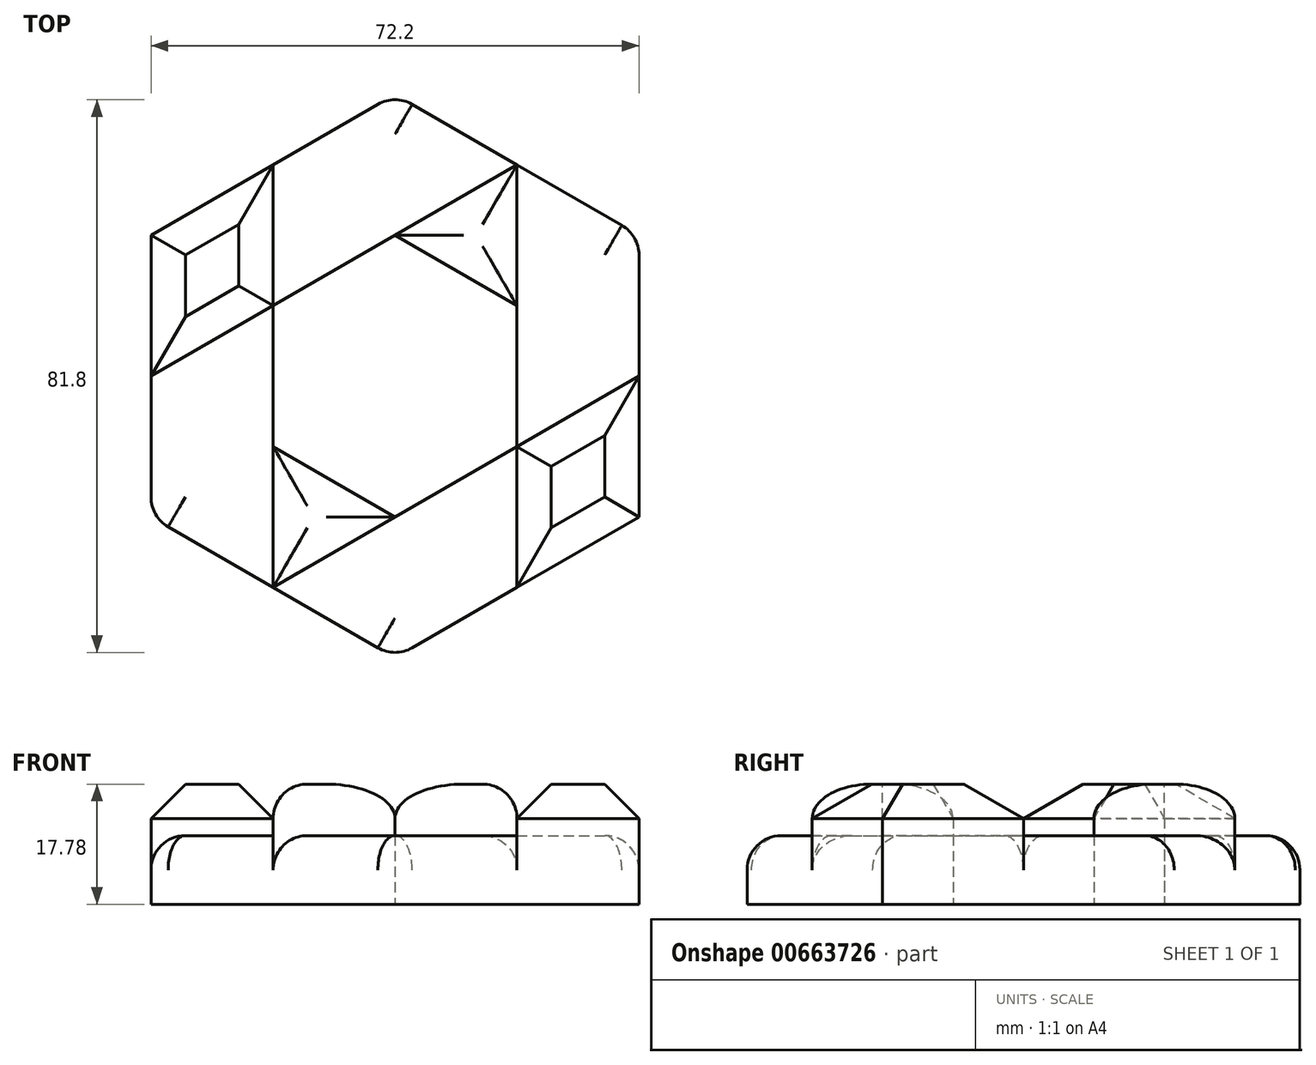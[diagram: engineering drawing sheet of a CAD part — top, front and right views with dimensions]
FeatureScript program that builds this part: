
annotation { "Feature Type Name" : "Feature", "Feature Type Description" : "" }
export const myFeature = defineFeature(function(context is Context, id is Id, definition is map)
    precondition{}
    {
        {
            var Q0;
            Q0=qCreatedBy(makeId("Top.planeOp"),FACE);
            var sketch = newSketch(context, id + "F0", { "sketchPlane" : qUnion([Q0])});
            skCircle(sketch, "E0.cCircle", {"center": v(0, 0) * mm, "radius": 36.1 * mm, "construction": true});
            skLineSegment(sketch, "E0.0", {"start": v(-36.1, -20.84) * mm, "end": v(-36.1, 20.84) * mm});
            skLineSegment(sketch, "E0.1", {"start": v(-36.1, 20.84) * mm, "end": v(0, 41.69) * mm});
            skLineSegment(sketch, "E0.2", {"start": v(0, 41.69) * mm, "end": v(36.1, 20.84) * mm});
            skLineSegment(sketch, "E0.3", {"start": v(36.1, 20.84) * mm, "end": v(36.1, -20.84) * mm});
            skLineSegment(sketch, "E0.4", {"start": v(36.1, -20.84) * mm, "end": v(0, -41.69) * mm});
            skLineSegment(sketch, "E0.5", {"start": v(0, -41.69) * mm, "end": v(-36.1, -20.84) * mm});
            skPoint(sketch, "E0.0.midPoint", {"position": v(-36.1, 0) * mm});
            skCircle(sketch, "E1.cCircle", {"center": v(0, 0) * mm, "radius": 18.05 * mm, "construction": true});
            skLineSegment(sketch, "E1.0", {"start": v(36.1, 0) * mm, "end": v(-18.05, -31.27) * mm});
            skLineSegment(sketch, "E1.1", {"start": v(-18.05, -31.27) * mm, "end": v(-18.05, 31.27) * mm});
            skLineSegment(sketch, "E1.2", {"start": v(-18.05, 31.27) * mm, "end": v(36.1, 0) * mm});
            skPoint(sketch, "E1.0.midPoint", {"position": v(9.03, -15.63) * mm});
            skLineSegment(sketch, "E2.0", {"start": v(-36.1, 0) * mm, "end": v(18.05, 31.27) * mm});
            skLineSegment(sketch, "E2.1", {"start": v(18.05, 31.27) * mm, "end": v(18.05, -31.27) * mm});
            skLineSegment(sketch, "E2.2", {"start": v(18.05, -31.27) * mm, "end": v(-36.1, 0) * mm});
            skPoint(sketch, "E2.0.midPoint", {"position": v(-9.03, 15.63) * mm});
            skSolve(sketch);
        }
        {
            var Q0;
            Q0 = qSketchRegion(id + "F0", true);
            extrude(context, id + "F1", {"entities" : qUnion([Q0]), "depth" : 10.16 * mm, "offsetDistance" : 25.4 * mm});
        }
        {
            var Q0;
            {var subQ1=sQuery(id+"F0.wireOp",EDGE,"E1.0");var subQ3=sQuery(id+"F0.wireOp",EDGE,"E2.2");var subQ4=makeQuery(id+"F0.imprint","INTERSECT",VERTEX,{"derivedFrom":[subQ1,subQ3]});Q0=makeQuery(id+"F0.imprint","IMPRINT",FACE,{"disambiguationData":[TD([[makeQuery(id+"F0.imprint","IMPRINT",EDGE,{"disambiguationData":[TD([[subQ4,-1.0]])],"derivedFrom":subQ3}),1.0]])]});}
            extrude(context, id + "F2", {"entities" : qUnion([Q0]), "operationType" : NewBodyOperationType.ADD, "depth" : 17.78 * mm, "offsetDistance" : 25.4 * mm});
        }
        {
            var Q0;
            {var subQ0=sQuery(id+"F0.wireOp",EDGE,"E2.0");var subQ1=sQuery(id+"F0.wireOp",EDGE,"E1.2");var subQ2=makeQuery(id+"F0.imprint","INTERSECT",VERTEX,{"derivedFrom":[subQ1,subQ0]});Q0=makeQuery(id+"F0.imprint","IMPRINT",FACE,{"disambiguationData":[TD([[makeQuery(id+"F0.imprint","IMPRINT",EDGE,{"disambiguationData":[TD([[subQ2,-1.0]])],"derivedFrom":subQ1}),1.0]])]});}
            extrude(context, id + "F3", {"entities" : qUnion([Q0]), "operationType" : NewBodyOperationType.ADD, "depth" : 17.78 * mm, "offsetDistance" : 25.4 * mm});
        }
        {
            var Q0;
            {var subQ0=sQuery(id+"F0.wireOp",EDGE,"E0.1");var subQ1=sQuery(id+"F0.wireOp",EDGE,"E0.0");var subQ2=makeQuery(id+"F0.imprint","INTERSECT",VERTEX,{"derivedFrom":[subQ1,subQ0]});Q0=makeQuery(id+"F0.imprint","IMPRINT",FACE,{"disambiguationData":[TD([[makeQuery(id+"F0.imprint","IMPRINT",EDGE,{"disambiguationData":[TD([[subQ2,1.0]])],"derivedFrom":subQ1}),-1.0]])]});}
            var Q1;
            {var subQ0=sQuery(id+"F0.wireOp",EDGE,"E0.4");var subQ1=sQuery(id+"F0.wireOp",EDGE,"E0.3");var subQ2=makeQuery(id+"F0.imprint","INTERSECT",VERTEX,{"derivedFrom":[subQ1,subQ0]});Q1=makeQuery(id+"F0.imprint","IMPRINT",FACE,{"disambiguationData":[TD([[makeQuery(id+"F0.imprint","IMPRINT",EDGE,{"disambiguationData":[TD([[subQ2,1.0]])],"derivedFrom":subQ1}),-1.0]])]});}
            extrude(context, id + "F4", {"entities" : qUnion([Q0, Q1]), "operationType" : NewBodyOperationType.ADD, "depth" : 17.78 * mm, "offsetDistance" : 25.4 * mm});
        }
        {
            var Q0;
            Q0=makeQuery(id+"F2.opExtrude","CAP_EDGE",EDGE,{"disambiguationData":[OSD([sQuery(id+"F0.wireOp",EDGE,"E1.0")])],"isStart":false});
            var Q1;
            Q1=makeQuery(id+"F2.opExtrude","CAP_EDGE",EDGE,{"disambiguationData":[OSD([sQuery(id+"F0.wireOp",EDGE,"E1.1")])],"isStart":false});
            var Q2;
            Q2=makeQuery(id+"F3.opExtrude","CAP_EDGE",EDGE,{"disambiguationData":[OSD([sQuery(id+"F0.wireOp",EDGE,"E1.2")])],"isStart":false});
            var Q3;
            Q3=makeQuery(id+"F3.opExtrude","CAP_EDGE",EDGE,{"disambiguationData":[OSD([sQuery(id+"F0.wireOp",EDGE,"E2.0")])],"isStart":false});
            var Q4;
            Q4=makeQuery(id+"F3.opExtrude","CAP_EDGE",EDGE,{"disambiguationData":[OSD([sQuery(id+"F0.wireOp",EDGE,"E2.1")])],"isStart":false});
            var Q5;
            Q5=makeQuery(id+"F2.opExtrude","CAP_EDGE",EDGE,{"disambiguationData":[OSD([sQuery(id+"F0.wireOp",EDGE,"E2.2")])],"isStart":false});
            fillet(context, id + "F5", {"entities" : qUnion([Q0, Q1, Q2, Q3, Q4, Q5]), "radius" : 5.08 * mm, "tangentPropagation" : true, "allowEdgeOverflow" : false});
        }
        {
            var Q0;
            Q0=makeQuery(id+"F4.opExtrude","CAP_EDGE",EDGE,{"disambiguationData":[OSD([sQuery(id+"F0.wireOp",EDGE,"E2.1")])],"isStart":false});
            var Q1;
            Q1=makeQuery(id+"F4.opExtrude","CAP_EDGE",EDGE,{"disambiguationData":[OSD([sQuery(id+"F0.wireOp",EDGE,"E1.0")])],"isStart":false});
            var Q2;
            Q2=makeQuery(id+"F4.opExtrude","CAP_EDGE",EDGE,{"disambiguationData":[OSD([sQuery(id+"F0.wireOp",EDGE,"E0.3")])],"isStart":false});
            var Q3;
            Q3=makeQuery(id+"F4.opExtrude","CAP_EDGE",EDGE,{"disambiguationData":[OSD([sQuery(id+"F0.wireOp",EDGE,"E0.4")])],"isStart":false});
            var Q4;
            Q4=makeQuery(id+"F4.opExtrude","CAP_EDGE",EDGE,{"disambiguationData":[OSD([sQuery(id+"F0.wireOp",EDGE,"E1.1")])],"isStart":false});
            var Q5;
            Q5=makeQuery(id+"F4.opExtrude","CAP_EDGE",EDGE,{"disambiguationData":[OSD([sQuery(id+"F0.wireOp",EDGE,"E2.0")])],"isStart":false});
            var Q6;
            Q6=makeQuery(id+"F4.opExtrude","CAP_EDGE",EDGE,{"disambiguationData":[OSD([sQuery(id+"F0.wireOp",EDGE,"E0.0")])],"isStart":false});
            var Q7;
            Q7=makeQuery(id+"F4.opExtrude","CAP_EDGE",EDGE,{"disambiguationData":[OSD([sQuery(id+"F0.wireOp",EDGE,"E0.1")])],"isStart":false});
            chamfer(context, id + "F6", {"entities" : qUnion([Q0, Q1, Q2, Q3, Q4, Q5, Q6, Q7]), "width" : 5.08 * mm, "tangentPropagation" : true});
        }
        {
            var Q0;
            {var subQ1=sQuery(id+"F0.wireOp",EDGE,"E0.2");var subQ2=sQuery(id+"F0.wireOp",EDGE,"E0.3");Q0=makeQuery(id+"F3.boolean.opBoolean","SPLIT",EDGE,{"disambiguationData":[TD([makeQuery(id+"F1.opExtrude","SWEPT_FACE",FACE,{"disambiguationData":[OSD([subQ2])]})])],"derivedFrom":makeQuery(id+"F1.opExtrude","CAP_EDGE",EDGE,{"disambiguationData":[OSD([subQ1])],"isStart":false})});}
            var Q1;
            {var subQ1=sQuery(id+"F0.wireOp",EDGE,"E0.2");var subQ2=sQuery(id+"F0.wireOp",EDGE,"E0.1");Q1=makeQuery(id+"F3.boolean.opBoolean","SPLIT",EDGE,{"disambiguationData":[TD([makeQuery(id+"F1.opExtrude","SWEPT_FACE",FACE,{"disambiguationData":[OSD([subQ2])]})])],"derivedFrom":makeQuery(id+"F1.opExtrude","CAP_EDGE",EDGE,{"disambiguationData":[OSD([subQ1])],"isStart":false})});}
            var Q2;
            {var subQ1=sQuery(id+"F0.wireOp",EDGE,"E0.5");var subQ3=sQuery(id+"F0.wireOp",EDGE,"E0.0");Q2=makeQuery(id+"F2.boolean.opBoolean","SPLIT",EDGE,{"disambiguationData":[TD([makeQuery(id+"F1.opExtrude","SWEPT_FACE",FACE,{"disambiguationData":[OSD([subQ3])]})])],"derivedFrom":makeQuery(id+"F1.opExtrude","CAP_EDGE",EDGE,{"disambiguationData":[OSD([subQ1])],"isStart":false})});}
            var Q3;
            {var subQ1=sQuery(id+"F0.wireOp",EDGE,"E0.4");var subQ2=sQuery(id+"F0.wireOp",EDGE,"E0.5");Q3=makeQuery(id+"F2.boolean.opBoolean","SPLIT",EDGE,{"disambiguationData":[TD([makeQuery(id+"F1.opExtrude","SWEPT_FACE",FACE,{"disambiguationData":[OSD([subQ1])]})])],"derivedFrom":makeQuery(id+"F1.opExtrude","CAP_EDGE",EDGE,{"disambiguationData":[OSD([subQ2])],"isStart":false})});}
            fillet(context, id + "F7", {"entities" : qUnion([Q0, Q1, Q2, Q3]), "radius" : 5.08 * mm, "tangentPropagation" : true, "allowEdgeOverflow" : false});
        }
        {
            var Q0;
            Q0=makeQuery(id+"F1.opExtrude","CAP_EDGE",EDGE,{"disambiguationData":[OSD([sQuery(id+"F0.wireOp",EDGE,"E0.1")])],"isStart":false});
            var Q1;
            Q1=makeQuery(id+"F1.opExtrude","CAP_EDGE",EDGE,{"disambiguationData":[OSD([sQuery(id+"F0.wireOp",EDGE,"E0.0")])],"isStart":false});
            var Q2;
            Q2=makeQuery(id+"F1.opExtrude","CAP_EDGE",EDGE,{"disambiguationData":[OSD([sQuery(id+"F0.wireOp",EDGE,"E0.4")])],"isStart":false});
            var Q3;
            Q3=makeQuery(id+"F1.opExtrude","CAP_EDGE",EDGE,{"disambiguationData":[OSD([sQuery(id+"F0.wireOp",EDGE,"E0.3")])],"isStart":false});
            fillet(context, id + "F8", {"entities" : qUnion([Q0, Q1, Q2, Q3]), "radius" : 5.08 * mm, "tangentPropagation" : true, "allowEdgeOverflow" : false});
        }
    });
